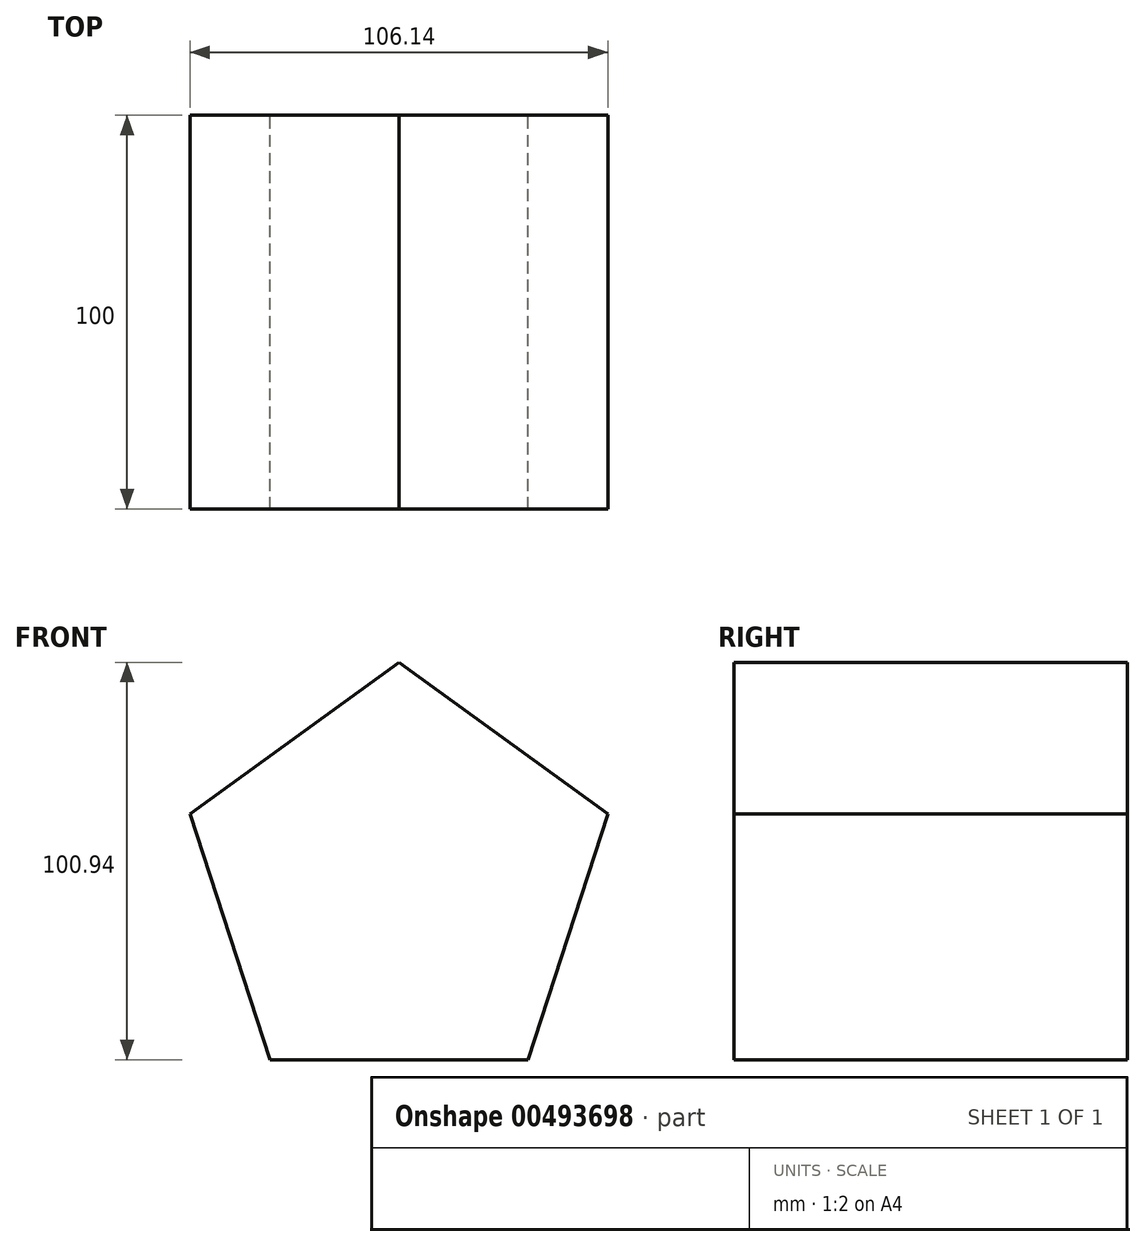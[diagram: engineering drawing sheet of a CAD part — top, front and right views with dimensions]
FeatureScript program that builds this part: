
annotation { "Feature Type Name" : "Feature", "Feature Type Description" : "" }
export const myFeature = defineFeature(function(context is Context, id is Id, definition is map)
    precondition{}
    {
        {
            var Q0;
            Q0=qCreatedBy(makeId("Front.planeOp"),FACE);
            var sketch = newSketch(context, id + "F0", { "sketchPlane" : qUnion([Q0])});
            skCircle(sketch, "E0.cCircle", {"center": v(0, 0) * mm, "radius": 55.8 * mm, "construction": true});
            skLineSegment(sketch, "E0.0", {"start": v(0, 55.8) * mm, "end": v(53.07, 17.24) * mm});
            skLineSegment(sketch, "E0.1", {"start": v(53.07, 17.24) * mm, "end": v(32.8, -45.14) * mm});
            skLineSegment(sketch, "E0.2", {"start": v(32.8, -45.14) * mm, "end": v(-32.8, -45.14) * mm});
            skLineSegment(sketch, "E0.3", {"start": v(-32.8, -45.14) * mm, "end": v(-53.07, 17.24) * mm});
            skLineSegment(sketch, "E0.4", {"start": v(-53.07, 17.24) * mm, "end": v(0, 55.8) * mm});
            skSolve(sketch);
        }
        {
            var Q0;
            Q0=makeQuery(id+"F0.imprint","IMPRINT",FACE,{"disambiguationData":[TD([[makeQuery(id+"F0.imprint","IMPRINT",EDGE,{"derivedFrom":sQuery(id+"F0.wireOp",EDGE,"E0.0")}),-1.0]])]});
            extrude(context, id + "F1", {"entities" : qUnion([Q0]), "depth" : 100 * mm});
        }
    });
